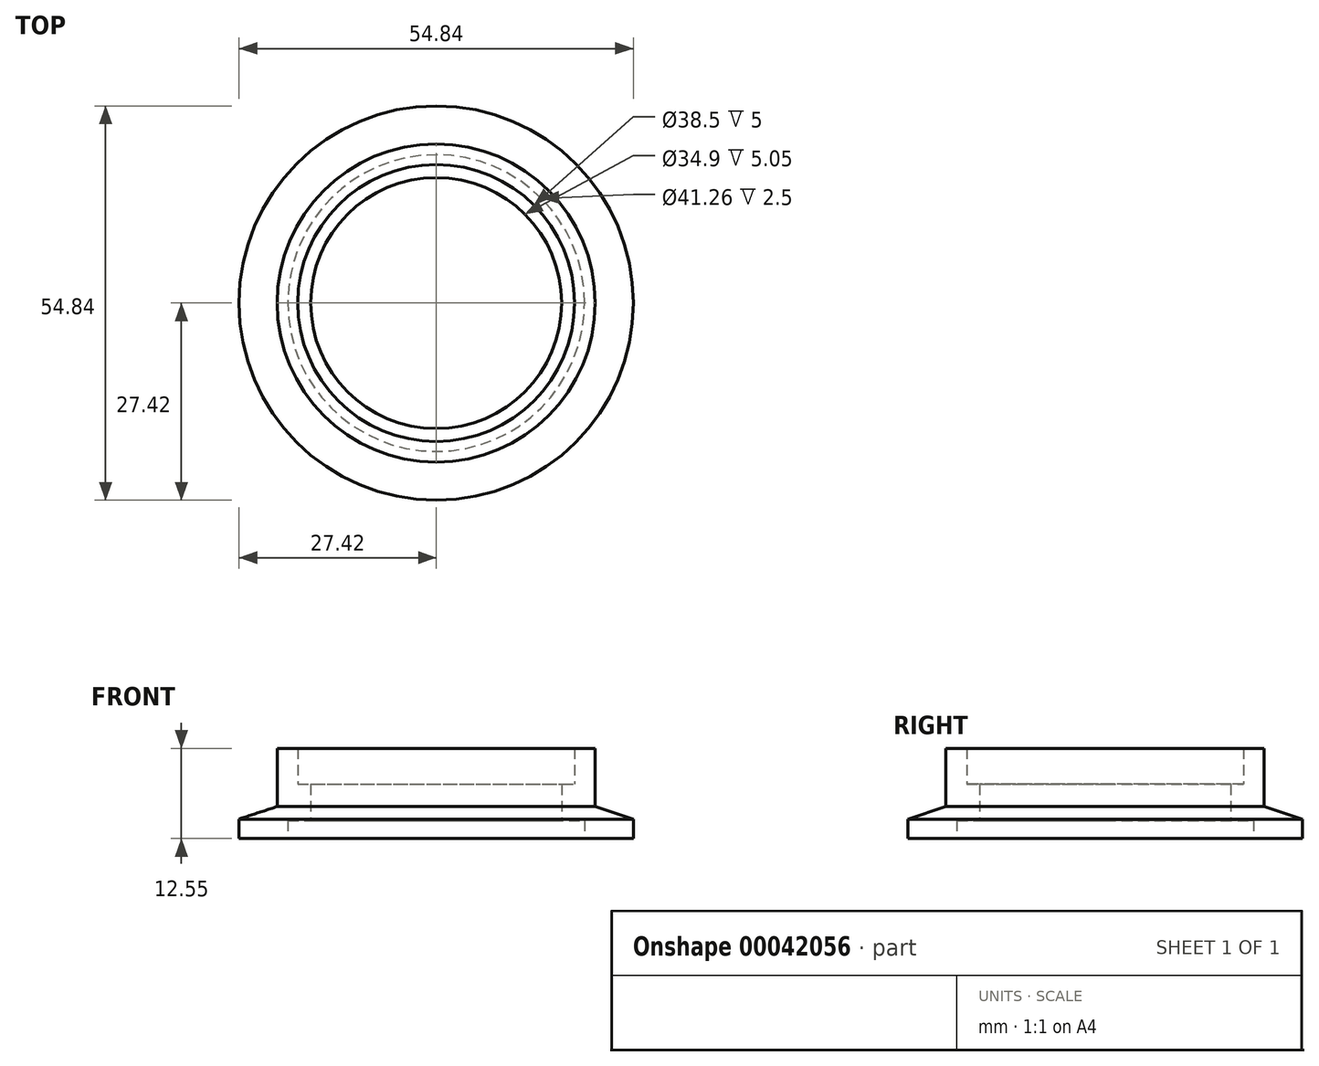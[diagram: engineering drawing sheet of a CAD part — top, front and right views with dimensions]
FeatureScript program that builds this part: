
annotation { "Feature Type Name" : "Feature", "Feature Type Description" : "" }
export const myFeature = defineFeature(function(context is Context, id is Id, definition is map)
    precondition{}
    {
        {
            var Q0;
            Q0=qCreatedBy(makeId("Front.planeOp"),FACE);
            var sketch = newSketch(context, id + "F0", { "sketchPlane" : qUnion([Q0])});
            skLineSegment(sketch, "E0", {"start": v(0, 0) * mm, "end": v(0, 12.55) * mm, "construction": true});
            skLineSegment(sketch, "E1", {"start": v(27.42, 0) * mm, "end": v(27.42, 2.7) * mm});
            skLineSegment(sketch, "E2", {"start": v(27.42, 2.7) * mm, "end": v(22.12, 4.45) * mm});
            skLineSegment(sketch, "E3", {"start": v(22.12, 4.45) * mm, "end": v(22.12, 12.55) * mm});
            skLineSegment(sketch, "E4", {"start": v(22.12, 12.55) * mm, "end": v(19.25, 12.55) * mm});
            skLineSegment(sketch, "E5", {"start": v(19.25, 12.55) * mm, "end": v(19.25, 7.55) * mm});
            skLineSegment(sketch, "E6", {"start": v(19.25, 7.55) * mm, "end": v(17.45, 7.55) * mm});
            skLineSegment(sketch, "E7", {"start": v(17.45, 7.55) * mm, "end": v(17.45, 2.5) * mm});
            skLineSegment(sketch, "E8", {"start": v(17.45, 2.5) * mm, "end": v(20.63, 2.5) * mm});
            skLineSegment(sketch, "E9", {"start": v(20.63, 2.5) * mm, "end": v(20.63, 0) * mm});
            skLineSegment(sketch, "E10", {"start": v(20.63, 0) * mm, "end": v(27.42, 0) * mm});
            skSolve(sketch);
        }
        {
            var Q0;
            Q0=makeQuery(id+"F0.imprint","IMPRINT",FACE,{"disambiguationData":[TD([[makeQuery(id+"F0.imprint","IMPRINT",EDGE,{"derivedFrom":sQuery(id+"F0.wireOp",EDGE,"E1")}),1.0]])]});
            var Q1;
            Q1=sQuery(id+"F0.wireOp",EDGE,"E0");
            revolve(context, id + "F1", {"entities" : qUnion([Q0]), "axis" : qUnion([Q1]), "revolveType" : RevolveType.FULL});
        }
    });
